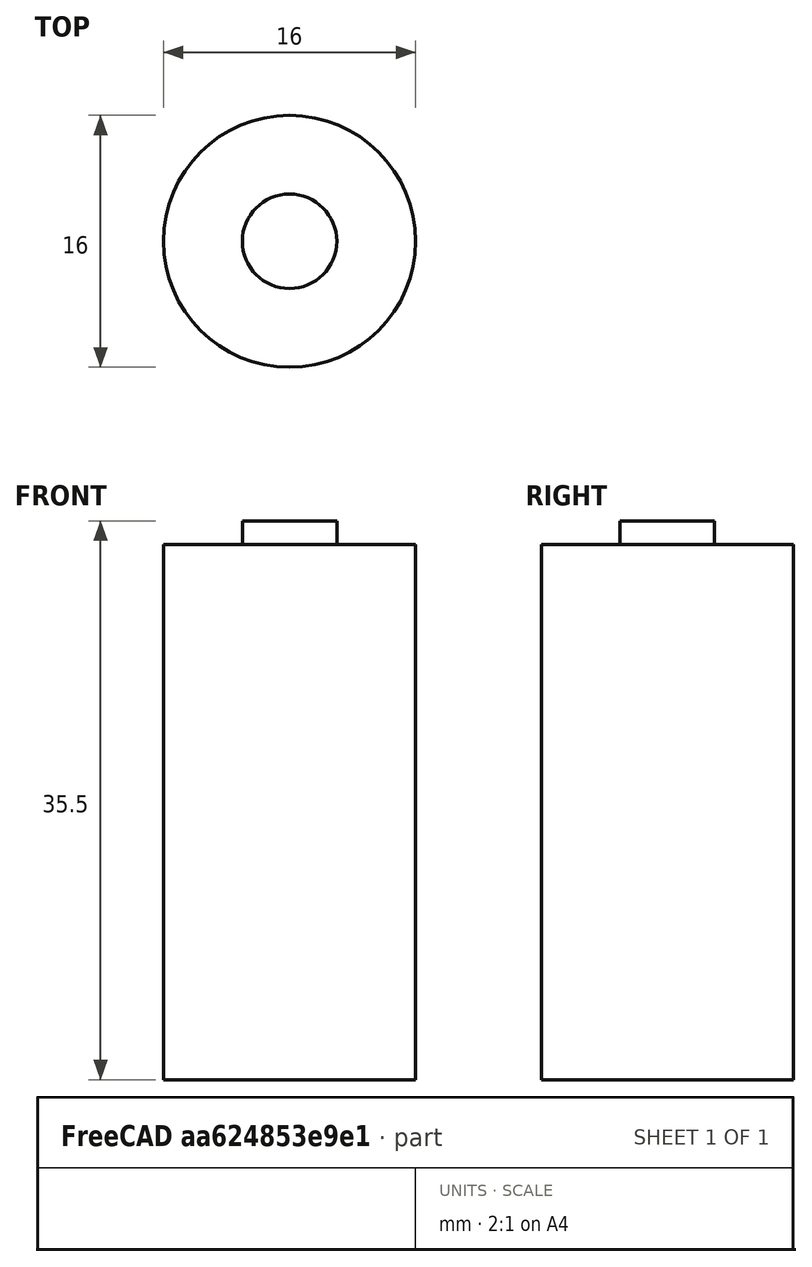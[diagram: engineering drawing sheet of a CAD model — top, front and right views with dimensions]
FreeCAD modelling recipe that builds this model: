
FCSTD DOCUMENT  (FreeCAD 0.19R24291 (Git))
Label: 16340-battery
License: All rights reserved
LicenseURL: http://en.wikipedia.org/wiki/All_rights_reserved
objects: PartDesign::AdditiveCylinder×2, PartDesign::CoordinateSystem×1, PartDesign::Body×1, App::Part×1
note: 6 computed .brp shape members not serialized (recipe doc carries the construction recipe); baked Part::Feature solids carry a one-line shape summary decoded from their .brp

FEATURE [PartDesign::CoordinateSystem] LCS_0
  AttacherType = Attacher::AttachEngine3D
  MapMode = 2
  Support = -> [X_Axis]
FEATURE [PartDesign::AdditiveCylinder] Cylinder  label="battery_cyl"
  Angle = 360
  AttacherType = Attacher::AttachEngine3D
  Height = 34
  MapMode = 5
  Radius = 8
  Support = -> [XY_Plane001]
FEATURE [PartDesign::AdditiveCylinder] Cylinder001  label="plus_cyl"
  Angle = 360
  AttacherType = Attacher::AttachEngine3D
  AttachmentOffset = pos=(0,0,34) rot=(0,0,1;0rad)
  BaseFeature = -> Cylinder
  Height = 1.5
  MapMode = 5
  Placement = pos=(0,0,34) rot=(0,0,1;0rad)
  Radius = 3
  Support = -> [XY_Plane001]
  expr: .AttachmentOffset.Base.z = <<battery_cyl>>.Height
FEATURE [PartDesign::Body] Body  label="battery_body"
  Group = -> [Cylinder,Cylinder001]
  Origin = -> Origin001
  Tip = -> Cylinder001
FEATURE [App::Part] _6340_battery_part  label="16340_battery_part"
  Group = -> [LCS_0,Body]
  Origin = -> Origin
